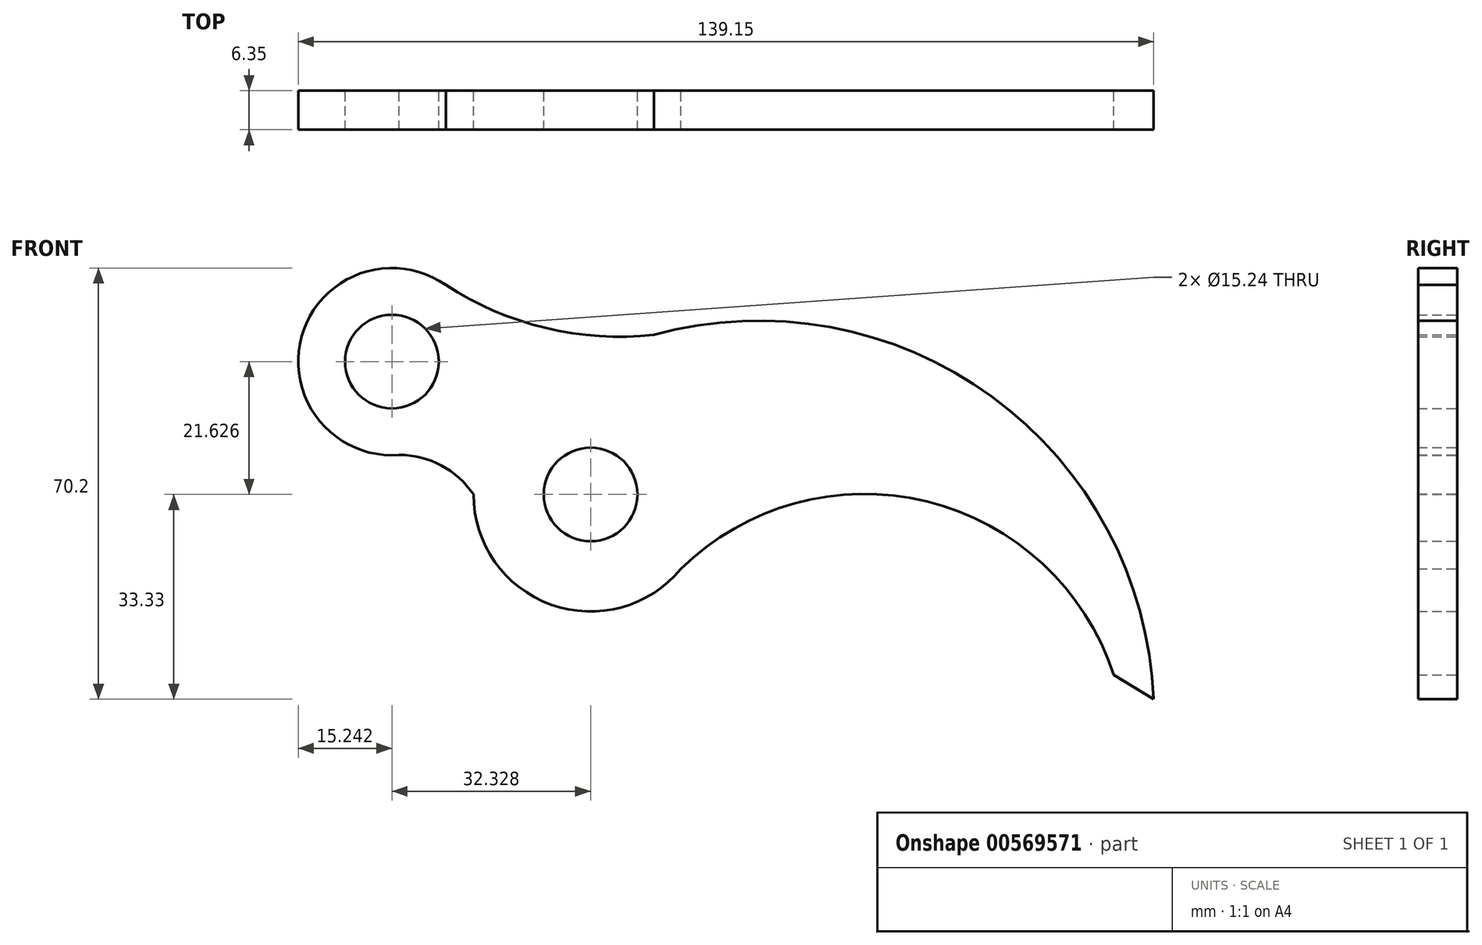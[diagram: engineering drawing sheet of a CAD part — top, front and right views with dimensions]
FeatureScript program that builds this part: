
annotation { "Feature Type Name" : "Feature", "Feature Type Description" : "" }
export const myFeature = defineFeature(function(context is Context, id is Id, definition is map)
    precondition{}
    {
        {
            var Q0;
            Q0=qCreatedBy(makeId("Front.planeOp"),FACE);
            var sketch = newSketch(context, id + "F0", { "sketchPlane" : qUnion([Q0])});
            skCircle(sketch, "E0", {"center": v(-56.35, 0) * mm, "radius": 7.62 * mm});
            skCircle(sketch, "E1", {"center": v(-56.35, 0) * mm, "radius": 19.05 * mm});
            skLineSegment(sketch, "E2", {"start": v(35.23, -33.33) * mm, "end": v(28.72, -29.37) * mm});
            skArc(sketch, "E3", {"start": v(28.72, -29.37) * mm, "mid": v(-2.99, -0.84) * mm, "end": v(-43.54, -14.1) * mm});
            skArc(sketch, "E4", {"start": v(35.23, -33.33) * mm, "mid": v(-1.59, 22.16) * mm, "end": v(-67.82, 15.2) * mm});
            skPoint(sketch, "E5.orphan", {"position": v(35.23, 0) * mm});
            skCircle(sketch, "E6", {"center": v(-88.68, 21.63) * mm, "radius": 7.62 * mm});
            skCircle(sketch, "E7", {"center": v(-88.68, 21.63) * mm, "radius": 15.24 * mm});
            skArc(sketch, "E8", {"start": v(-80.61, 34.56) * mm, "mid": v(-64.09, 27.2) * mm, "end": v(-46.05, 25.97) * mm});
            skArc(sketch, "E9", {"start": v(-75.4, 0) * mm, "mid": v(-81.18, 4.99) * mm, "end": v(-88.68, 6.39) * mm});
            skSolve(sketch);
        }
        {
            var Q0;
            Q0 = qSketchRegion(id + "F0", true);
            extrude(context, id + "F1", {"entities" : qUnion([Q0]), "depth" : 6.35 * mm, "offsetDistance" : 25.4 * mm});
        }
    });
